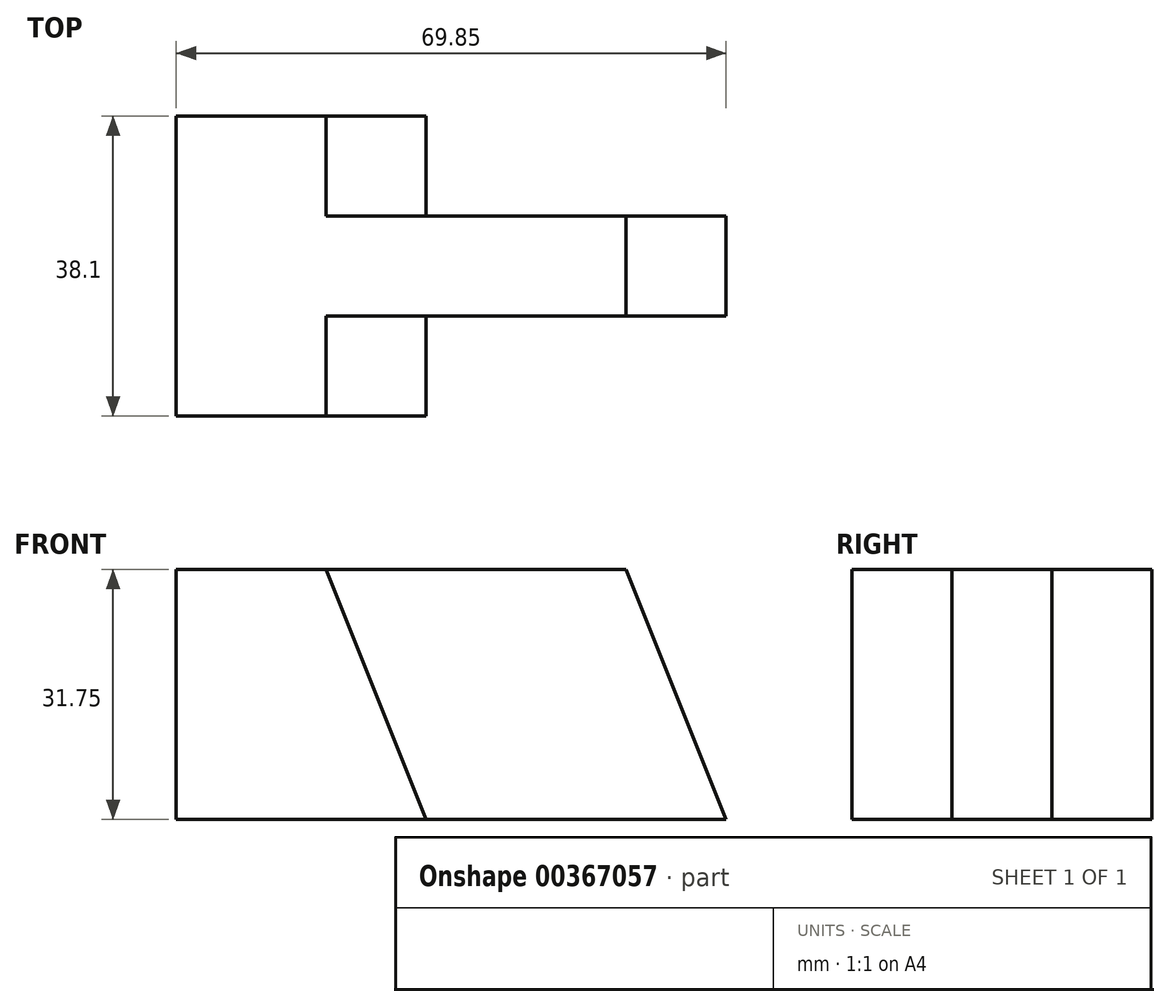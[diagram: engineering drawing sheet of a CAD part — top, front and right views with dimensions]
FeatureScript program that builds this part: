
annotation { "Feature Type Name" : "Feature", "Feature Type Description" : "" }
export const myFeature = defineFeature(function(context is Context, id is Id, definition is map)
    precondition{}
    {
        {
            var Q0;
            Q0=qCreatedBy(makeId("Front.planeOp"),FACE);
            var sketch = newSketch(context, id + "F0", { "sketchPlane" : qUnion([Q0])});
            skLineSegment(sketch, "E0", {"start": v(-69.85, 31.75) * mm, "end": v(0, 31.75) * mm});
            skLineSegment(sketch, "E1", {"start": v(0, 31.75) * mm, "end": v(0, 0) * mm});
            skLineSegment(sketch, "E2", {"start": v(0, 0) * mm, "end": v(-69.85, 0) * mm});
            skLineSegment(sketch, "E3", {"start": v(-69.85, 0) * mm, "end": v(-69.85, 31.75) * mm});
            skSolve(sketch);
        }
        {
            var Q0;
            Q0=makeQuery(id+"F0.imprint","IMPRINT",FACE,{"disambiguationData":[TD([[makeQuery(id+"F0.imprint","IMPRINT",EDGE,{"derivedFrom":sQuery(id+"F0.wireOp",EDGE,"E0")}),-1.0]])]});
            extrude(context, id + "F1", {"entities" : qUnion([Q0]), "depth" : 38.1 * mm});
        }
        {
            var Q0;
            Q0=makeQuery(id+"F1.opExtrude","CAP_FACE",FACE,{"disambiguationData":[OSD([sQuery(id+"F0.wireOp",EDGE,"E0"),sQuery(id+"F0.wireOp",EDGE,"E1"),sQuery(id+"F0.wireOp",EDGE,"E2"),sQuery(id+"F0.wireOp",EDGE,"E3")])],"isStart":false});
            var sketch = newSketch(context, id + "F2", { "sketchPlane" : qUnion([Q0])});
            skLineSegment(sketch, "E4", {"start": v(-50.8, 31.75) * mm, "end": v(-38.1, 0) * mm});
            skLineSegment(sketch, "E5", {"start": v(-50.8, 31.75) * mm, "end": v(0, 31.75) * mm});
            skLineSegment(sketch, "E6", {"start": v(0, 31.75) * mm, "end": v(0, 0) * mm});
            skLineSegment(sketch, "E7", {"start": v(0, 0) * mm, "end": v(-38.1, 0) * mm});
            skSolve(sketch);
        }
        {
            var Q0;
            Q0=makeQuery(id+"F2.imprint","IMPRINT",FACE,{"disambiguationData":[TD([[makeQuery(id+"F2.imprint","IMPRINT",EDGE,{"derivedFrom":sQuery(id+"F2.wireOp",EDGE,"E4")}),1.0]])]});
            extrude(context, id + "F3", {"entities" : qUnion([Q0]), "operationType" : NewBodyOperationType.REMOVE, "oppositeDirection" : true, "depth" : 12.7 * mm});
        }
        {
            var Q0;
            Q0=makeQuery(id+"F1.opExtrude","CAP_FACE",FACE,{"disambiguationData":[OSD([sQuery(id+"F0.wireOp",EDGE,"E0"),sQuery(id+"F0.wireOp",EDGE,"E1"),sQuery(id+"F0.wireOp",EDGE,"E2"),sQuery(id+"F0.wireOp",EDGE,"E3")])],"isStart":true});
            var sketch = newSketch(context, id + "F4", { "sketchPlane" : qUnion([Q0])});
            skLineSegment(sketch, "E8", {"start": v(38.1, 0) * mm, "end": v(50.8, 31.75) * mm});
            skLineSegment(sketch, "E9", {"start": v(50.8, 31.75) * mm, "end": v(0, 31.75) * mm});
            skLineSegment(sketch, "E10", {"start": v(0, 31.75) * mm, "end": v(0, 0) * mm});
            skLineSegment(sketch, "E11", {"start": v(0, 0) * mm, "end": v(38.1, 0) * mm});
            skLineSegment(sketch, "E12", {"start": v(38.1, 0) * mm, "end": v(0, 0) * mm});
            skSolve(sketch);
        }
        {
            var Q0;
            Q0=makeQuery(id+"F4.imprint","IMPRINT",FACE,{"disambiguationData":[TD([[makeQuery(id+"F4.imprint","IMPRINT",EDGE,{"derivedFrom":sQuery(id+"F4.wireOp",EDGE,"E8")}),1.0]])]});
            extrude(context, id + "F5", {"entities" : qUnion([Q0]), "operationType" : NewBodyOperationType.REMOVE, "oppositeDirection" : true, "depth" : 12.7 * mm});
        }
        {
            var Q0;
            Q0=makeQuery(id+"F3.boolean.opBoolean","COPY",FACE,{"derivedFrom":makeQuery(id+"F3.opExtrude","CAP_FACE",FACE,{"disambiguationData":[OSD([sQuery(id+"F2.wireOp",EDGE,"E4"),sQuery(id+"F2.wireOp",EDGE,"E5"),sQuery(id+"F2.wireOp",EDGE,"E6"),sQuery(id+"F2.wireOp",EDGE,"E7")])],"isStart":false})});
            var sketch = newSketch(context, id + "F6", { "sketchPlane" : qUnion([Q0])});
            skLineSegment(sketch, "E13", {"start": v(0, 0) * mm, "end": v(-12.7, 31.75) * mm});
            skLineSegment(sketch, "E14", {"start": v(-12.7, 31.75) * mm, "end": v(0, 31.75) * mm});
            skLineSegment(sketch, "E15", {"start": v(0, 31.75) * mm, "end": v(0, 0) * mm});
            skSolve(sketch);
        }
        {
            var Q0;
            Q0=makeQuery(id+"F6.imprint","IMPRINT",FACE,{"disambiguationData":[TD([[makeQuery(id+"F6.imprint","IMPRINT",EDGE,{"derivedFrom":sQuery(id+"F6.wireOp",EDGE,"E13")}),-1.0]])]});
            extrude(context, id + "F7", {"entities" : qUnion([Q0]), "operationType" : NewBodyOperationType.REMOVE, "oppositeDirection" : true, "depth" : 12.7 * mm});
        }
    });
